# Revit family: JOMA_Balksko Special_40 ̸ 60
name_source: partatom
category: Structural Connections
revit_build: Autodesk Revit Structure 2012 (Build: 20110309_2315(x64)
units: mm (PartAtom-declared; Revit-internal decimal feet)

## types (1)
- 40/60
    Default Elevation = 1219 mm
    H140 = H140
    H160 = H160
    H180 = H180
    H200 = H200
    H220 = H220
    H240 = H240
    H260 = H260
    H280 = H280
    H300 = H300
    H320 = H320
    H340 = H340
    H360 = H360
    H380 = H380
    H400 = H400
    H420 = H420
    H440 = H440
    H460 = H460
    H480 = H480
    H500 = H500
    Länk Joma Dimensioneringsverktyg = http://www.joma.se
    Material = Varmförzinkad stålplåt
    Typ = TYP 40/60
    Typ 40 ̸ 60 = Yes
    X = 40 mm  [stored 0.131234 ft]
    Y = 60 mm  [stored 0.19685 ft]

note: [stored X ft] marks values corroborated as IEEE doubles in the binary element streams (Revit-internal decimal feet)

## geometry (parser evidence)
native form markers: Sweep x44
no freeform markers — native parametric forms only
